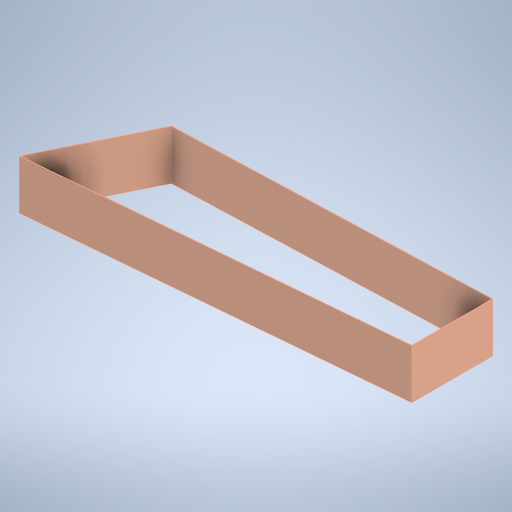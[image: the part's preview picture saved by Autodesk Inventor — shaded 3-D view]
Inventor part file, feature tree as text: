
AUTODESK INVENTOR PART (.ipt)
format: ipt  version: 2024 (Build 280153020, 153B)  size: 244,224 bytes
history: native  units: in
note: dims shown in document units (in); Inventor stores cm internally (conversion verified against a paired STEP export)
features: extrude x1, sketch x1
ambient origin geometry x8: Origin, YZ Plane, XZ Plane, XY Plane, X Axis, Y Axis, Z Axis, Center Point
bodies: Solid1 (feature_tree)
feature tree (2):
  extrude  "Extrusion1"  Depth=336.0in
  sketch  "Sketch1"  dims[d0=2463.341in d3=2113.33in d5=0.6533in d6=0.6048in d7=551.48in d8=4.25in d9=336.0in d10=0.0in d11=0.5in d12=0.0344in d13=0.5in d14=0.0344in]
